# Revit family: Haworth_ActiveComponents_120HalfWrapAround_Reside_BUILD
name_source: partatom
category: Furniture Systems
revit_build: Autodesk Revit Architecture 2015 (Build: 20141119_1515(x64)
units: mm (PartAtom-declared; Revit-internal decimal feet)

## types (1)
- 57w 24d
    Actual Depth = 24"
    Actual Height = 29 3/16"
    Actual Width = 48"
    Angled Leg Side Offset = 17 3/4"
    Assembly Code = E2020200
    Description = Haworth - Worksurface - 120 Half Wrap Around - Reside
    Half Width = 12"
    Manufacturer = Haworth
    Model = WKYM
    Radius = 60"
    Revision Number = 1
    Screen Depth Opening = 1 13/16"
    Screen Mounting Height = 28"
    Screen Width = 48"
    Size = Verify Final Dim. w/ Haworth
    Support Height = 28"
    Sustainability Info = https://www.haworth.com
    URL = www.haworth.com
    URL - Product = https://www.haworth.com
    Warranty = http://www.haworth.com
    With Leg = Yes
    With Screen = Yes
    Worksurface Thickness = 1 3/16"

## geometry (parser evidence)
native form markers: Blend x90, Sweep x14
no freeform markers — native parametric forms only
